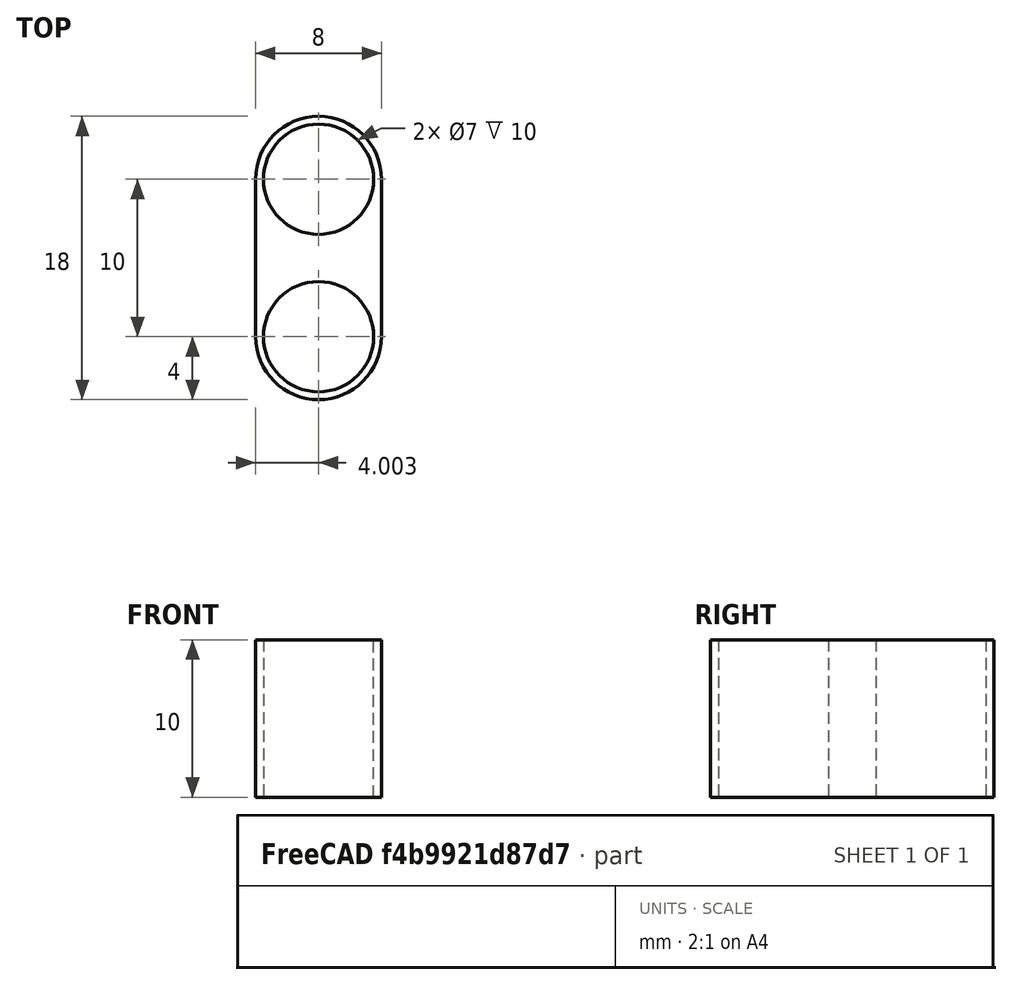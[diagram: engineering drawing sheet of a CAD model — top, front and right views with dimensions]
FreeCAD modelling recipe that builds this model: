
FCSTD DOCUMENT  (FreeCAD 0.19R24415 (Git))
Label: led-shield
License: All rights reserved
LicenseURL: http://en.wikipedia.org/wiki/All_rights_reserved
objects: Sketcher::SketchObject×1, PartDesign::Pad×1, PartDesign::Body×1
note: 4 computed .brp shape members not serialized (recipe doc carries the construction recipe); baked Part::Feature solids carry a one-line shape summary decoded from their .brp

FEATURE [Sketcher::SketchObject] Sketch010
  FullyConstrained = false
  sketch-geometry (6):
    g0: Circle CenterX=-122.917 CenterY=25.7898 CenterZ=0 NormalX=0 NormalY=0 NormalZ=1 AngleXU=0 Radius=3.5
    g1: Circle CenterX=-122.917 CenterY=15.7898 CenterZ=0 NormalX=0 NormalY=0 NormalZ=1 AngleXU=0 Radius=3.5
    g2: ArcOfCircle CenterX=-122.917 CenterY=25.7898 CenterZ=0 NormalX=0 NormalY=0 NormalZ=1 AngleXU=0 Radius=4 StartAngle=5e-16 EndAngle=3.14159
    g3: ArcOfCircle CenterX=-122.917 CenterY=15.7898 CenterZ=0 NormalX=0 NormalY=0 NormalZ=1 AngleXU=0 Radius=4 StartAngle=3.14159 EndAngle=6.28319
    g4: LineSegment StartX=-126.917 StartY=25.7898 StartZ=0 EndX=-126.917 EndY=15.7898 EndZ=0
    g5: LineSegment StartX=-118.917 StartY=25.7898 StartZ=0 EndX=-118.917 EndY=15.7898 EndZ=0
  constraints (13):
    c: Radius(g0) = 3.5
    c: Equal(g0,g1)
    c: DistanceY(g1,g0) = 10
    c: Vertical(g0,g1)
    c: Tangent(g2,g5) = 1.5708
    c: Tangent(g2,g4) = -1.5708
    c: Tangent(g4,g3) = -1.5708
    c: Tangent(g5,g3) = 1.5708
    c: Vertical(g4)
    c: Equal(g2,g3)
    c: Coincident(g2,g0)
    c: Horizontal(g1,g3)
    c: Radius(g2) = 4
FEATURE [PartDesign::Pad] Pad001
  Direction = (1,1,1)
  Length = 10
  Length2 = 100
  Profile = -> Sketch010
  Type = 0
FEATURE [PartDesign::Body] Body002  label="LED Shield"
  Group = -> [Sketch010,Pad001]
  Origin = -> Origin003
  Tip = -> Pad001
